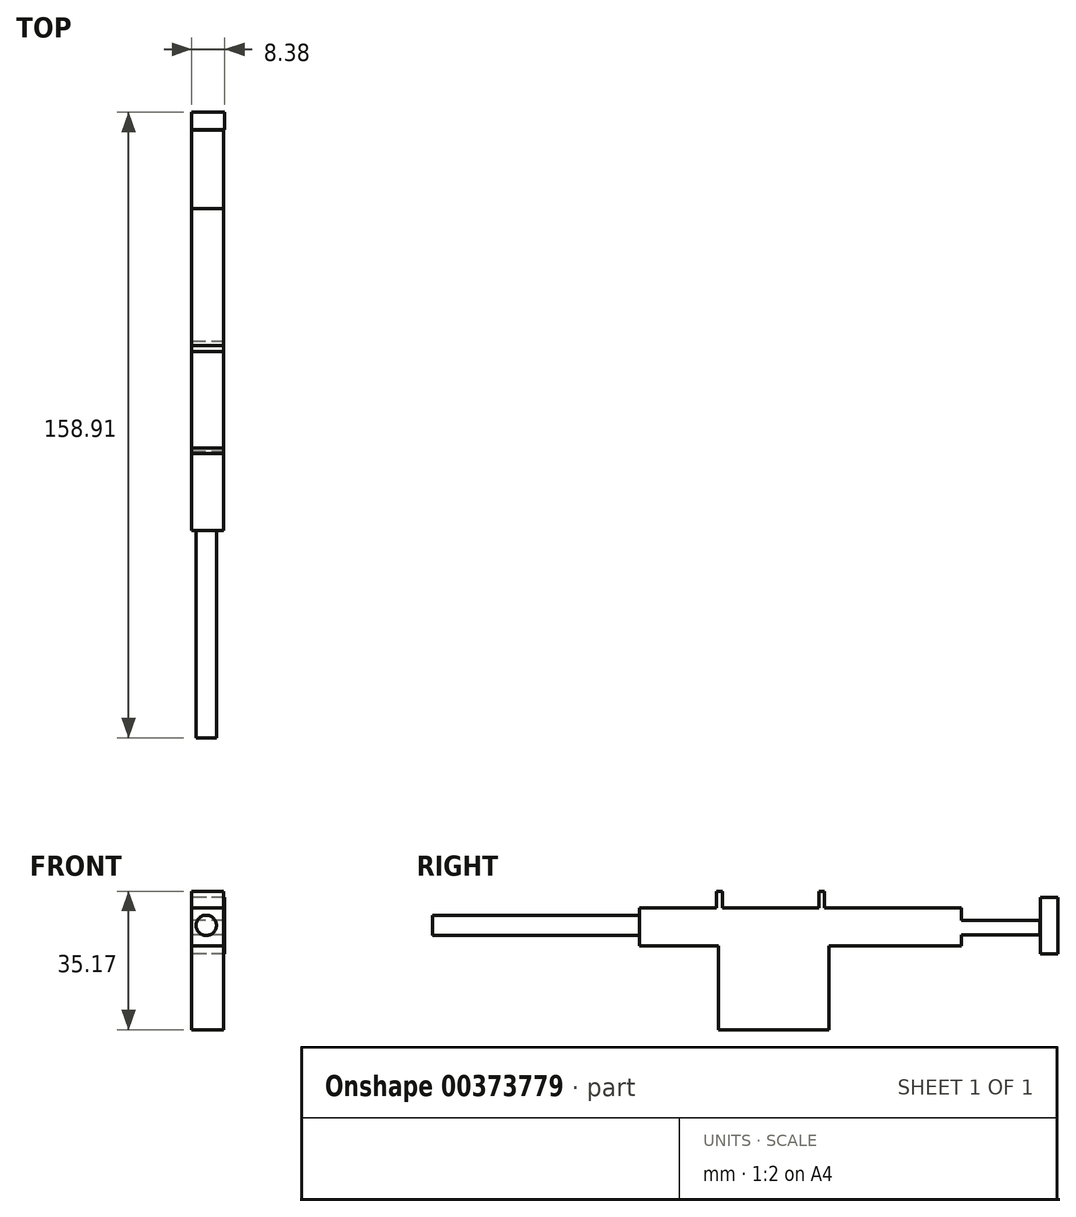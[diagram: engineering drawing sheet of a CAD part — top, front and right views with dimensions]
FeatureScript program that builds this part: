
annotation { "Feature Type Name" : "Feature", "Feature Type Description" : "" }
export const myFeature = defineFeature(function(context is Context, id is Id, definition is map)
    precondition{}
    {
        {
            var Q0;
            Q0=qCreatedBy(makeId("Right.planeOp"),FACE);
            var sketch = newSketch(context, id + "F0", { "sketchPlane" : qUnion([Q0])});
            skLineSegment(sketch, "E0.bottom", {"start": v(-13.13, 0) * mm, "end": v(14.86, 0) * mm});
            skLineSegment(sketch, "E0.top", {"start": v(-13.13, -21.3) * mm, "end": v(14.86, -21.3) * mm});
            skLineSegment(sketch, "E0.left", {"start": v(-13.13, 0) * mm, "end": v(-13.13, -21.3) * mm});
            skLineSegment(sketch, "E0.right", {"start": v(14.86, 0) * mm, "end": v(14.86, -21.3) * mm});
            skSolve(sketch);
        }
        {
            var Q0;
            Q0 = qSketchRegion(id + "F0", true);
            extrude(context, id + "F1", {"entities" : qUnion([Q0]), "depth" : 8.13 * mm});
        }
        {
            var Q0;
            Q0=qCreatedBy(makeId("Right.planeOp"),FACE);
            var sketch = newSketch(context, id + "F2", { "sketchPlane" : qUnion([Q0])});
            skLineSegment(sketch, "E1.bottom", {"start": v(-33.2, 0) * mm, "end": v(48.55, 0) * mm});
            skLineSegment(sketch, "E1.top", {"start": v(-33.2, 9.66) * mm, "end": v(48.55, 9.66) * mm});
            skLineSegment(sketch, "E1.left", {"start": v(-33.2, 0) * mm, "end": v(-33.2, 9.66) * mm});
            skLineSegment(sketch, "E1.right", {"start": v(48.55, 0) * mm, "end": v(48.55, 9.66) * mm});
            skSolve(sketch);
        }
        {
            var Q0;
            Q0 = qSketchRegion(id + "F2", true);
            extrude(context, id + "F3", {"entities" : qUnion([Q0]), "operationType" : NewBodyOperationType.ADD, "depth" : 8.13 * mm});
        }
        {
            var Q0;
            Q0=qCreatedBy(makeId("Front.planeOp"),FACE);
            var sketch = newSketch(context, id + "F4", { "sketchPlane" : qUnion([Q0])});
            skCircle(sketch, "E2", {"center": v(3.72, 5.2) * mm, "radius": 2.59 * mm});
            skSolve(sketch);
        }
        {
            var Q0;
            Q0 = qSketchRegion(id + "F4", true);
            extrude(context, id + "F5", {"entities" : qUnion([Q0]), "operationType" : NewBodyOperationType.ADD, "depth" : 85.85 * mm});
        }
        {
            var Q0;
            Q0=qCreatedBy(makeId("Right.planeOp"),FACE);
            var sketch = newSketch(context, id + "F6", { "sketchPlane" : qUnion([Q0])});
            skLineSegment(sketch, "E3.bottom", {"start": v(-13.68, 9.17) * mm, "end": v(-12.2, 9.17) * mm});
            skLineSegment(sketch, "E3.top", {"start": v(-13.68, 13.87) * mm, "end": v(-12.2, 13.87) * mm});
            skLineSegment(sketch, "E3.left", {"start": v(-13.68, 9.17) * mm, "end": v(-13.68, 13.87) * mm});
            skLineSegment(sketch, "E3.right", {"start": v(-12.2, 9.17) * mm, "end": v(-12.2, 13.87) * mm});
            skLineSegment(sketch, "E4.bottom", {"start": v(13.82, 9.41) * mm, "end": v(12.33, 9.41) * mm});
            skLineSegment(sketch, "E4.top", {"start": v(13.82, 13.87) * mm, "end": v(12.33, 13.87) * mm});
            skLineSegment(sketch, "E4.left", {"start": v(13.82, 9.41) * mm, "end": v(13.82, 13.87) * mm});
            skLineSegment(sketch, "E4.right", {"start": v(12.33, 9.41) * mm, "end": v(12.33, 13.87) * mm});
            skSolve(sketch);
        }
        {
            var Q0;
            Q0 = qSketchRegion(id + "F6", true);
            extrude(context, id + "F7", {"entities" : qUnion([Q0]), "operationType" : NewBodyOperationType.ADD, "depth" : 8.13 * mm});
        }
        {
            var Q0;
            Q0=qCreatedBy(makeId("Right.planeOp"),FACE);
            var sketch = newSketch(context, id + "F8", { "sketchPlane" : qUnion([Q0])});
            skLineSegment(sketch, "E5.bottom", {"start": v(48.43, 6.44) * mm, "end": v(68.5, 6.44) * mm});
            skLineSegment(sketch, "E5.top", {"start": v(48.43, 2.72) * mm, "end": v(68.5, 2.72) * mm});
            skLineSegment(sketch, "E5.left", {"start": v(48.43, 6.44) * mm, "end": v(48.43, 2.72) * mm});
            skLineSegment(sketch, "E5.right", {"start": v(68.5, 6.44) * mm, "end": v(68.5, 2.72) * mm});
            skSolve(sketch);
        }
        {
            var Q0;
            Q0 = qSketchRegion(id + "F8", true);
            extrude(context, id + "F9", {"entities" : qUnion([Q0]), "operationType" : NewBodyOperationType.ADD, "depth" : 8.13 * mm});
        }
        {
            var Q0;
            Q0=qCreatedBy(makeId("Right.planeOp"),FACE);
            var sketch = newSketch(context, id + "F10", { "sketchPlane" : qUnion([Q0])});
            skLineSegment(sketch, "E6.bottom", {"start": v(68.6, -1.99) * mm, "end": v(73.06, -1.99) * mm});
            skLineSegment(sketch, "E6.top", {"start": v(68.6, 12.36) * mm, "end": v(73.06, 12.36) * mm});
            skLineSegment(sketch, "E6.left", {"start": v(68.6, -1.99) * mm, "end": v(68.6, 12.36) * mm});
            skLineSegment(sketch, "E6.right", {"start": v(73.06, -1.99) * mm, "end": v(73.06, 12.36) * mm});
            skPoint(sketch, "E6.middle", {"position": v(70.83, 5.18) * mm});
            skSolve(sketch);
        }
        {
            var Q0;
            Q0 = qSketchRegion(id + "F10", true);
            extrude(context, id + "F11", {"entities" : qUnion([Q0]), "depth" : 8.38 * mm});
        }
    });
